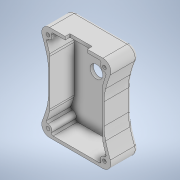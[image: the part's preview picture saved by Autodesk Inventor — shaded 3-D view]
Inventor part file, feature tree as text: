
AUTODESK INVENTOR PART (.ipt)
format: ipt  version: 2021 (Build 250183000, 183)  size: 402,944 bytes
history: native  units: mm
features: extrude x8, sketch x8, mirror x7, fillet x6, shell x2, projected_geometry x2
ambient origin geometry x8: Origin, YZ Plane, XZ Plane, XY Plane, X Axis, Y Axis, Z Axis, Center Point
bodies: Solid1 (feature_tree)
feature tree (33):
  extrude  "Extrusion1"  Depth=17.25mm
  shell  "Shell1"  Thickness=17.25mm
  extrude  "Extrusion2"  Depth=75.0mm
  mirror  "Mirror1"
  mirror  "Mirror2"
  fillet  "Fillet2"  Radius=20.0mm
  fillet  "Fillet3"  Radius=75.0mm
  shell  "Shell2"  Thickness=16.75mm
  extrude  "Extrusion3"  Depth=5.0mm
  mirror  "Mirror3"
  mirror  "Mirror4"
  fillet  "Fillet4"  Radius=5.0mm
  extrude  "Extrusion4"  Depth=2.5mm
  extrude  "Extrusion5"  Depth=1.0mm
  mirror  "Mirror5"
  mirror  "Mirror6"
  fillet  "Fillet5"  Radius=1.0mm
  extrude  "Extrusion6"  Depth=1.0mm
  extrude  "Extrusion8"  Depth=8.0mm
  fillet  "Fillet6"  Radius=8.0mm
  extrude  "Extrusion10"  Depth=8.0mm
  fillet  "Fillet7"  [1 undecoded]
  mirror  "Mirror7"
  sketch  "Sketch1"  dims[d0=35.0mm d1=60.0mm d2=17.25mm d3=0.0mm]
  sketch  "Sketch2"  dims[d4=2.0mm d5=7.0mm d7=20.0mm d8=75.0mm d9=16.75mm d10=0.0mm]
  sketch  "Sketch3"  dims[d12=2.0mm d13=30.0mm d14=5.0mm]
  sketch  "Sketch4"  dims[d15=2.0mm d18=2.5mm]
  sketch  "Sketch5"  dims[d19=5.0mm d20=2.2mm d21=1.0mm]
  sketch  "Sketch6"  dims[d22=10.0mm d23=0.0mm d24=1.0mm]
  sketch  "Sketch8"  dims[d25=0.0mm d26=0.0mm d27=3.75mm d28=8.0mm d29=0.0mm]
  sketch  "Sketch10"  dims[d30=1.0mm d31=8.0mm d34=0.0mm d35=0.0mm d37=5.4mm d40=1.1mm d41=10.0mm d42=0.0mm d43=5.0mm d46=14.0mm d47=3.0mm d48=10.0mm d49=0.0mm d50=0.5mm d51=2.54mm]
  projected_geometry  "Project Cut Edges1"
  projected_geometry  "Project Cut Edges2"
note: 1 required parameter value undecoded (feature->parameter linkage not recoverable at this tier; creation-order binding heuristic only, values carry confidence <= 0.55)
